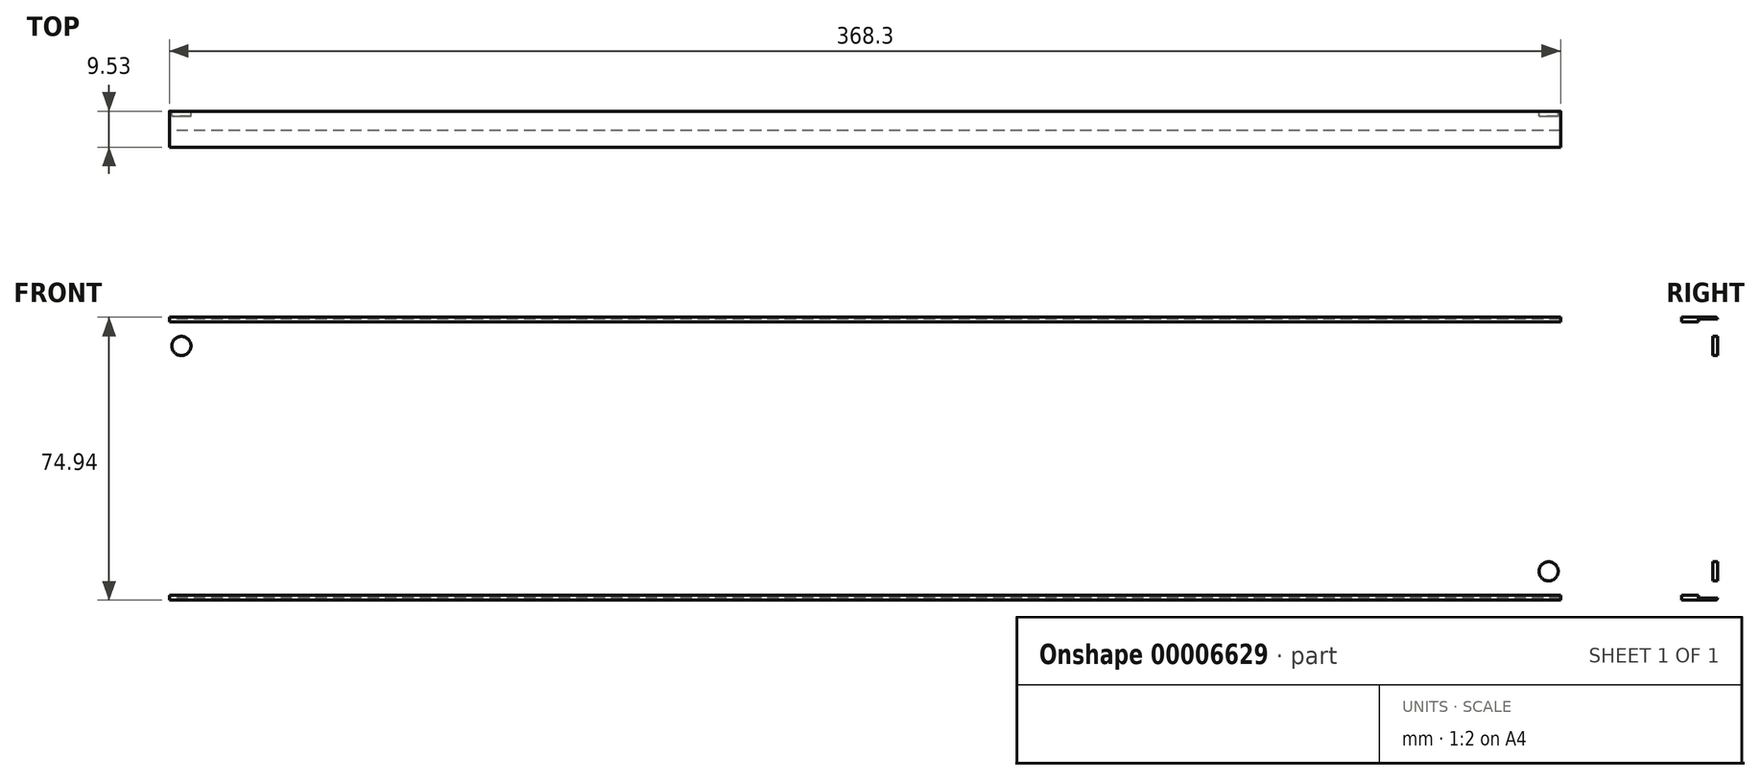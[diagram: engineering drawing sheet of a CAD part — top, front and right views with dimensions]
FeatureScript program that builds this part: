
annotation { "Feature Type Name" : "Feature", "Feature Type Description" : "" }
export const myFeature = defineFeature(function(context is Context, id is Id, definition is map)
    precondition{}
    {
        {
            var Q0;
            Q0=qCreatedBy(makeId("Right.planeOp"),FACE);
            var sketch = newSketch(context, id + "F0", { "sketchPlane" : qUnion([Q0])});
            skLineSegment(sketch, "E0", {"start": v(0, -36.96) * mm, "end": v(0, 36.96) * mm});
            skLineSegment(sketch, "E1", {"start": v(-0.5, 37.47) * mm, "end": v(-9.53, 37.47) * mm});
            skLineSegment(sketch, "E2", {"start": v(-9.53, 37.47) * mm, "end": v(-9.53, 36.2) * mm});
            skLineSegment(sketch, "E3", {"start": v(-9.53, 36.2) * mm, "end": v(-1.27, 36.2) * mm});
            skLineSegment(sketch, "E4", {"start": v(-1.27, 36.2) * mm, "end": v(-1.27, -36.2) * mm});
            skLineSegment(sketch, "E5", {"start": v(-1.27, -36.2) * mm, "end": v(-9.52, -36.2) * mm});
            skLineSegment(sketch, "E6", {"start": v(-9.52, -36.2) * mm, "end": v(-9.52, -37.47) * mm});
            skLineSegment(sketch, "E7", {"start": v(-9.52, -37.47) * mm, "end": v(-0.5, -37.47) * mm});
            skPoint(sketch, "E8.visualSharp", {"position": v(0, 37.47) * mm});
            skArc(sketch, "E8.filletArc", {"start": v(0, 36.96) * mm, "mid": v(-0.15, 37.32) * mm, "end": v(-0.5, 37.47) * mm});
            skPoint(sketch, "E9.visualSharp", {"position": v(0, -37.47) * mm});
            skArc(sketch, "E9.filletArc", {"start": v(-0.5, -37.46) * mm, "mid": v(-0.15, -37.32) * mm, "end": v(0, -36.96) * mm});
            skSolve(sketch);
        }
        {
            var Q0;
            Q0=makeQuery(id+"F0.imprint","IMPRINT",FACE,{"disambiguationData":[TD([[makeQuery(id+"F0.imprint","IMPRINT",EDGE,{"derivedFrom":sQuery(id+"F0.wireOp",EDGE,"E0")}),1.0]])]});
            extrude(context, id + "F1", {"entities" : qUnion([Q0]), "endBound" : BoundingType.SYMMETRIC, "depth" : 368.3 * mm});
        }
        {
            var Q0;
            Q0=makeQuery(id+"F1.opExtrude","SWEPT_FACE",FACE,{"disambiguationData":[OSD([sQuery(id+"F0.wireOp",EDGE,"E0")])]});
            var sketch = newSketch(context, id + "F2", { "sketchPlane" : qUnion([Q0])});
            skCircle(sketch, "E10", {"center": v(-180.98, 29.84) * mm, "radius": 2.54 * mm});
            skCircle(sketch, "E11.0.MirrorC", {"center": v(180.98, 29.84) * mm, "radius": 2.54 * mm});
            skLineSegment(sketch, "E12", {"start": v(-209.65, 0) * mm, "end": v(190.64, 0) * mm, "construction": true});
            skCircle(sketch, "E13.0.MirrorC", {"center": v(-180.98, -29.84) * mm, "radius": 2.54 * mm});
            skCircle(sketch, "E14.0.MirrorC", {"center": v(180.98, -29.84) * mm, "radius": 2.54 * mm});
            skSolve(sketch);
        }
        {
            var Q0;
            Q0=makeQuery(id+"F2.imprint","IMPRINT",FACE,{"disambiguationData":[TD([[makeQuery(id+"F2.imprint","IMPRINT",EDGE,{"derivedFrom":sQuery(id+"F2.wireOp",EDGE,"E10")}),1.0]])]});
            var Q1;
            Q1=makeQuery(id+"F2.imprint","IMPRINT",FACE,{"disambiguationData":[TD([[makeQuery(id+"F2.imprint","IMPRINT",EDGE,{"derivedFrom":sQuery(id+"F2.wireOp",EDGE,"E13.0.MirrorC")}),-1.0]])]});
            var Q2;
            Q2=makeQuery(id+"F2.imprint","IMPRINT",FACE,{"disambiguationData":[TD([[makeQuery(id+"F2.imprint","IMPRINT",EDGE,{"derivedFrom":sQuery(id+"F2.wireOp",EDGE,"E11.0.MirrorC")}),-1.0]])]});
            var Q3;
            Q3=makeQuery(id+"F2.imprint","IMPRINT",FACE,{"disambiguationData":[TD([[makeQuery(id+"F2.imprint","IMPRINT",EDGE,{"derivedFrom":sQuery(id+"F2.wireOp",EDGE,"E14.0.MirrorC")}),1.0]])]});
            var Q4;
            Q4=sQuery(id+"F2.wireOp",EDGE,"E10");
            var Q5;
            Q5=sQuery(id+"F2.wireOp",EDGE,"E13.0.MirrorC");
            var Q6;
            Q6=sQuery(id+"F2.wireOp",EDGE,"E11.0.MirrorC");
            var Q7;
            Q7=sQuery(id+"F2.wireOp",EDGE,"E14.0.MirrorC");
            extrude(context, id + "F3", {"entities" : qUnion([Q0, Q1, Q2, Q3]), "operationType" : NewBodyOperationType.REMOVE, "surfaceEntities" : qUnion([Q4, Q5, Q6, Q7]), "oppositeDirection" : true, "depth" : 5.08 * mm});
        }
    });
